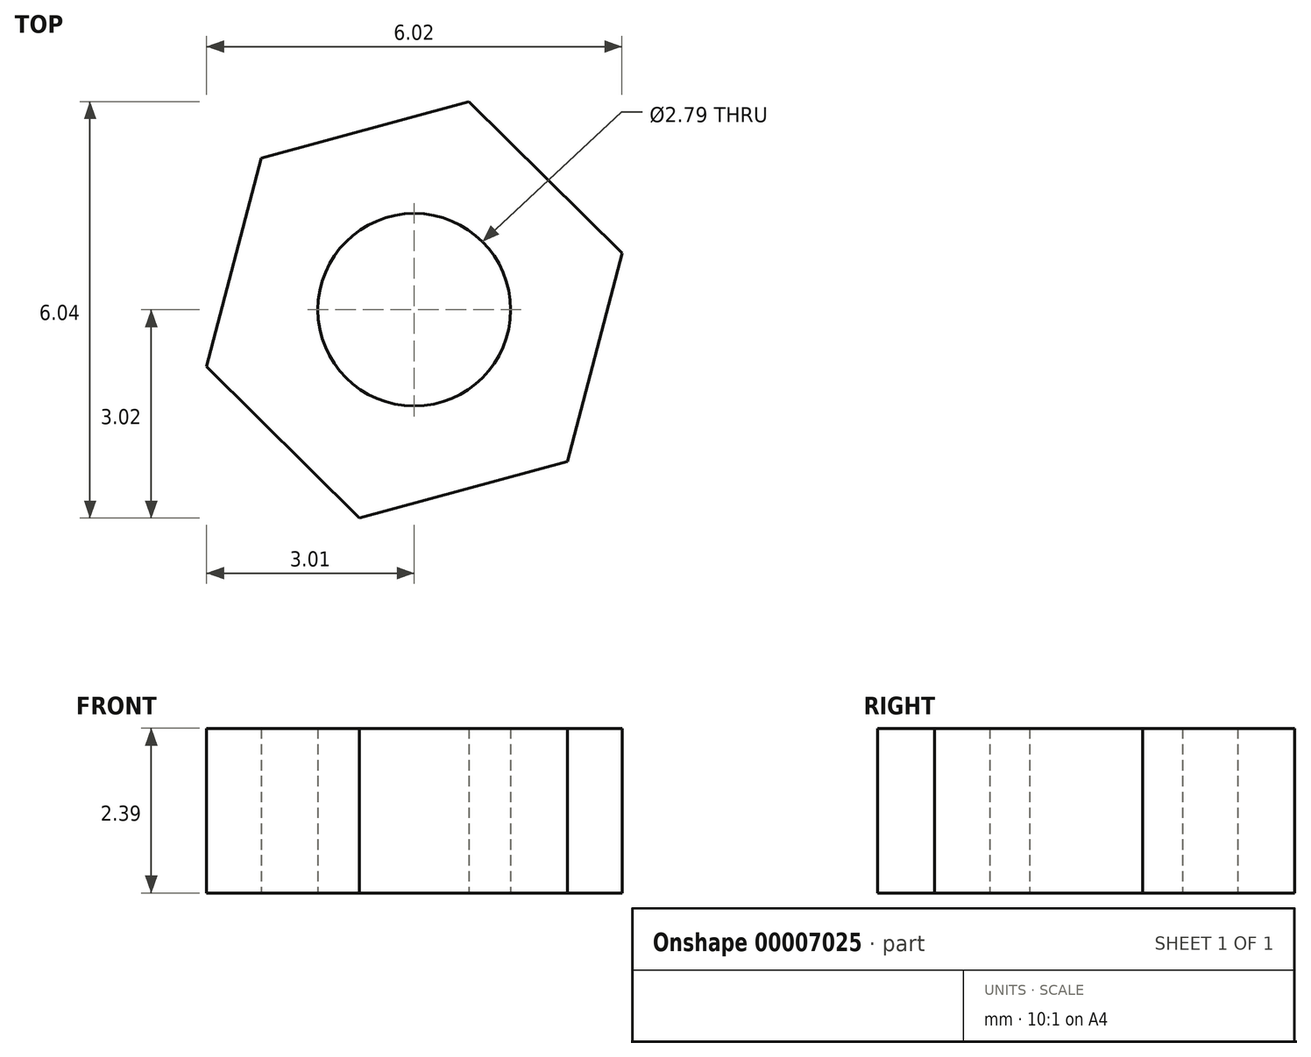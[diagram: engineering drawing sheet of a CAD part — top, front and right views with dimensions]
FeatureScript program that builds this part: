
annotation { "Feature Type Name" : "Feature", "Feature Type Description" : "" }
export const myFeature = defineFeature(function(context is Context, id is Id, definition is map)
    precondition{}
    {
        {
            var Q0;
            Q0=qCreatedBy(makeId("Top.planeOp"),FACE);
            var sketch = newSketch(context, id + "F0", { "sketchPlane" : qUnion([Q0])});
            skCircle(sketch, "E0.cCircle", {"center": v(0, 0) * mm, "radius": 2.7 * mm, "construction": true});
            skLineSegment(sketch, "E0.0", {"start": v(3.01, 0.82) * mm, "end": v(2.22, -2.2) * mm});
            skLineSegment(sketch, "E0.1", {"start": v(2.22, -2.2) * mm, "end": v(-0.8, -3.02) * mm});
            skLineSegment(sketch, "E0.2", {"start": v(-0.8, -3.02) * mm, "end": v(-3.01, -0.82) * mm});
            skLineSegment(sketch, "E0.3", {"start": v(-3.01, -0.82) * mm, "end": v(-2.22, 2.2) * mm});
            skLineSegment(sketch, "E0.4", {"start": v(-2.22, 2.2) * mm, "end": v(0.8, 3.02) * mm});
            skLineSegment(sketch, "E0.5", {"start": v(0.8, 3.02) * mm, "end": v(3.01, 0.82) * mm});
            skPoint(sketch, "E0.0.midPoint", {"position": v(2.62, -0.69) * mm});
            skCircle(sketch, "E1", {"center": v(0, 0) * mm, "radius": 1.4 * mm});
            skSolve(sketch);
        }
        {
            var Q0;
            Q0=makeQuery(id+"F0.imprint","IMPRINT",FACE,{"disambiguationData":[TD([[makeQuery(id+"F0.imprint","IMPRINT",EDGE,{"derivedFrom":sQuery(id+"F0.wireOp",EDGE,"E0.0")}),-1.0]])]});
            extrude(context, id + "F1", {"entities" : qUnion([Q0]), "depth" : 2.4 * mm});
        }
        {
            var Q0;
            Q0=makeQuery(id+"F0.imprint","IMPRINT",FACE,{"disambiguationData":[TD([[makeQuery(id+"F0.imprint","IMPRINT",EDGE,{"derivedFrom":sQuery(id+"F0.wireOp",EDGE,"E1")}),1.0]])]});
            extrude(context, id + "F2", {"entities" : qUnion([Q0]), "operationType" : NewBodyOperationType.REMOVE, "oppositeDirection" : true, "depth" : 25.4 * mm});
        }
    });
